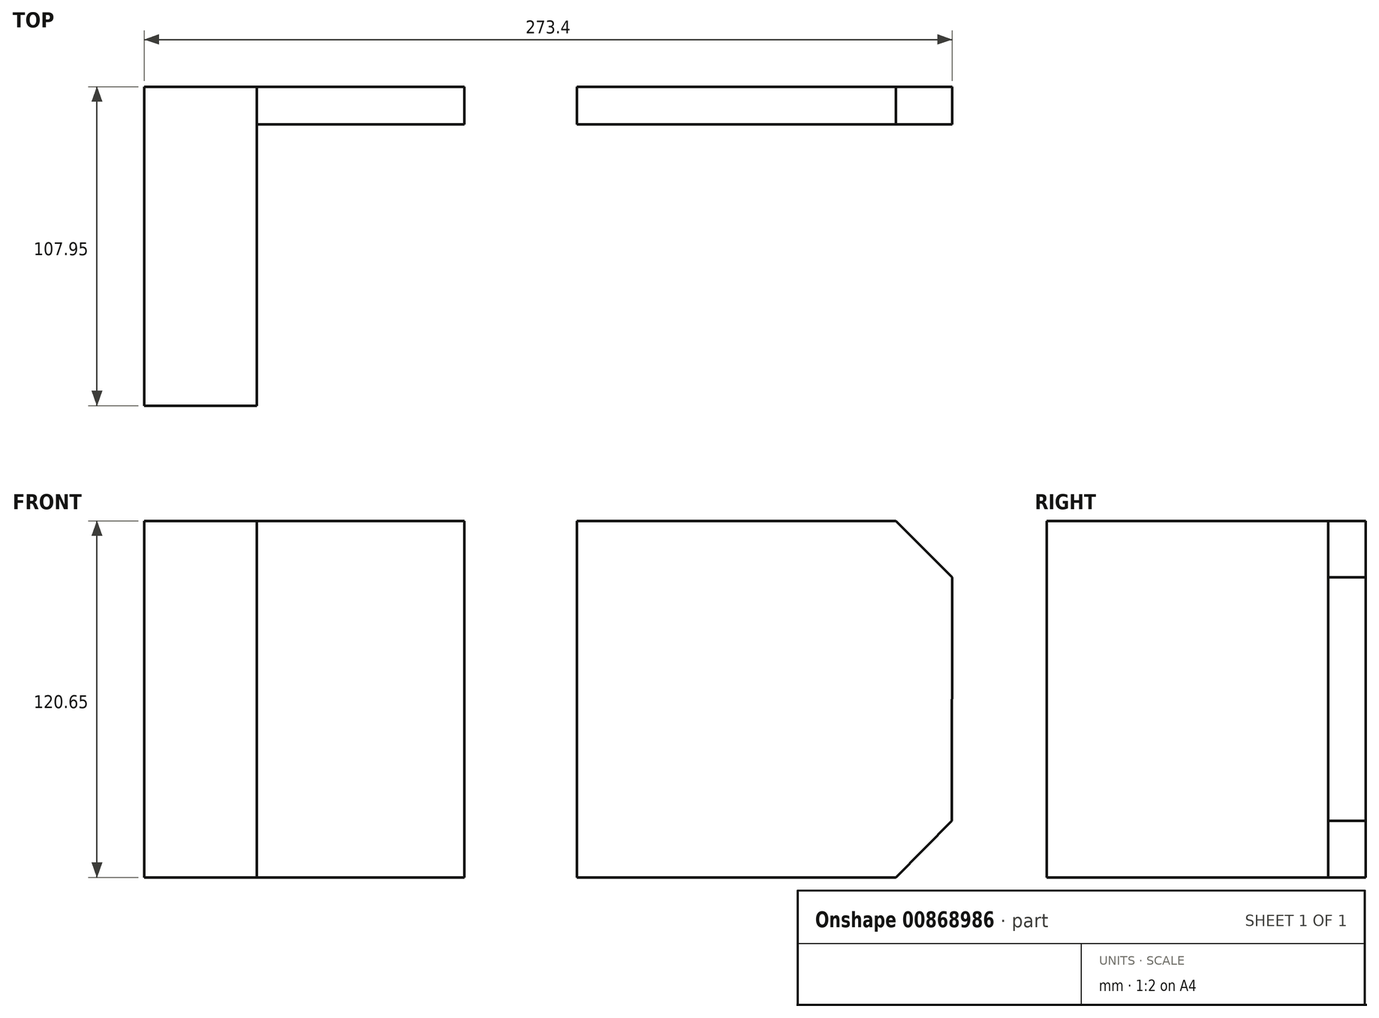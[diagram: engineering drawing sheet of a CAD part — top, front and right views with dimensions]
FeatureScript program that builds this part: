
annotation { "Feature Type Name" : "Feature", "Feature Type Description" : "" }
export const myFeature = defineFeature(function(context is Context, id is Id, definition is map)
    precondition{}
    {
        {
            var Q0;
            Q0=qCreatedBy(makeId("Front.planeOp"),FACE);
            var sketch = newSketch(context, id + "F0", { "sketchPlane" : qUnion([Q0])});
            skLineSegment(sketch, "E0", {"start": v(0, 0) * mm, "end": v(-112.9, 0) * mm});
            skLineSegment(sketch, "E1", {"start": v(-38.45, 120.65) * mm, "end": v(215.9, 120.65) * mm});
            skLineSegment(sketch, "E2", {"start": v(215.9, 120.65) * mm, "end": v(234.95, 101.6) * mm});
            skLineSegment(sketch, "E3", {"start": v(215.9, 0) * mm, "end": v(0, 0) * mm});
            skLineSegment(sketch, "E4", {"start": v(-38.45, 120.65) * mm, "end": v(-38.45, 0) * mm});
            skLineSegment(sketch, "E5", {"start": v(-38.45, 0) * mm, "end": v(-0.35, 0) * mm});
            skLineSegment(sketch, "E6", {"start": v(-0.35, 0) * mm, "end": v(-0.35, 120.65) * mm});
            skLineSegment(sketch, "E7", {"start": v(69.85, 0) * mm, "end": v(107.95, 0) * mm});
            skLineSegment(sketch, "E8", {"start": v(107.95, 0) * mm, "end": v(107.95, 120.65) * mm});
            skLineSegment(sketch, "E9", {"start": v(-112.9, 0) * mm, "end": v(-112.9, 38.1) * mm});
            skLineSegment(sketch, "E10", {"start": v(-112.9, 38.1) * mm, "end": v(-38.45, 120.65) * mm});
            skLineSegment(sketch, "E11", {"start": v(69.85, 0) * mm, "end": v(69.85, 120.65) * mm});
            skLineSegment(sketch, "E12", {"start": v(215.9, 0) * mm, "end": v(234.85, 19.15) * mm});
            skLineSegment(sketch, "E13", {"start": v(234.95, 101.6) * mm, "end": v(234.85, 19.15) * mm});
            skSolve(sketch);
        }
        {
            var Q0;
            {var subQ0=sQuery(id+"F0.wireOp",EDGE,"mgQv68gC-bmhz-xsxm-Ybhz-vIPApdTaedc5");Q0=makeQuery(id+"F0.imprint","IMPRINT",FACE,{"disambiguationData":[TD([[makeQuery(id+"F0.imprint","IMPRINT",EDGE,{"derivedFrom":subQ0}),-1.0]])]});}
            var Q1;
            {var subQ0=sQuery(id+"F0.wireOp",EDGE,"E6");Q1=makeQuery(id+"F0.imprint","IMPRINT",FACE,{"disambiguationData":[TD([[makeQuery(id+"F0.imprint","IMPRINT",EDGE,{"derivedFrom":subQ0}),-1.0]])]});}
            var Q2;
            {var subQ4=sQuery(id+"F0.wireOp",EDGE,"6V3mrlgH-CnF8-H6sZ-oj3t-GcH6VP0PYZO5");Q2=makeQuery(id+"F0.imprint","IMPRINT",FACE,{"disambiguationData":[TD([[makeQuery(id+"F0.imprint","IMPRINT",EDGE,{"derivedFrom":subQ4}),-1.0]])]});}
            var Q3;
            {var subQ1=sQuery(id+"F0.wireOp",EDGE,"E2");Q3=makeQuery(id+"F0.imprint","IMPRINT",FACE,{"disambiguationData":[TD([[makeQuery(id+"F0.imprint","IMPRINT",EDGE,{"derivedFrom":subQ1}),-1.0]])]});}
            extrude(context, id + "F1", {"entities" : qUnion([Q0, Q1, Q2, Q3]), "depth" : 12.7 * mm, "offsetDistance" : 25.4 * mm});
        }
        {
            var Q0;
            {var subQ3=sQuery(id+"F0.wireOp",EDGE,"7kFqgkU4-bsi6-mbra-59MV-yuHmqq9atrXN");Q0=makeQuery(id+"F0.imprint","IMPRINT",FACE,{"disambiguationData":[TD([[makeQuery(id+"F0.imprint","IMPRINT",EDGE,{"derivedFrom":subQ3}),1.0]])]});}
            var Q1;
            {var subQ0=sQuery(id+"F0.wireOp",EDGE,"E4");Q1=makeQuery(id+"F0.imprint","IMPRINT",FACE,{"disambiguationData":[TD([[makeQuery(id+"F0.imprint","IMPRINT",EDGE,{"derivedFrom":subQ0}),1.0]])]});}
            extrude(context, id + "F2", {"entities" : qUnion([Q0, Q1]), "depth" : 107.95 * mm, "offsetDistance" : 25.4 * mm});
        }
    });
